# Revit family: RAR3
name_source: partatom
category: Lighting Fixtures
revit_build: Autodesk Revit 2014 (Build: 20130308_1515(x64)
units: mm (PartAtom-declared; Revit-internal decimal feet)

## types (1)
- RAR3
    Apparent Load = 40 VA
    Assembly Code = D5020200
    Center Width = 3 "
    Certifications = UL,CSA,Wet Listed, Damp Listed, ANSI 3G Vibration Rated
    Color Filter = 16777215
    Color Temperature = 0 K
    Depth = 18.44 "
    Description = With a new spin on a classic rectilinear form, Ratio brings the traditional shoebox aesthetic into the next generation of LED lighting. Ratio features a dense optical array which provides reduced pixilation and increased visual comfort without compromising performance. Designed for sustained, long-term performance with advanced thermal management, an elegantly simple heat sink, and industry leading surge protection.
    Dimming Lamp Color Temperature Shift = <None>
    Emit Shape Visible in Rendering = No
    Emit from Rectangle Length = 15 "
    Emit from Rectangle Width = 15 "
    Features = • Low profile LED area/site luminaire with a variety of IES distributions for
lighting applications such as retail, commercial and campus parking lots
• Featuring Micro Strike Optics which maximizes target zone illumination with
minimal losses at the house-side, reducing light trespass issues
• Visual comfort standard
• Area and flood optics available for maximum versatility
• Control options including photo control, occupancy sensing, NX Distributed
Intelligence™ and 7-Pin with networked controls
• Best in class surge protection
    Finish = Powder Coat-Hubbell-Black
    Fixture Height = 7.5 "
    Lamp = default
    Lens = Glass-Hubbell-Temper Molded
    Manufacturer = Hubbell Lighting
    Model = RAR3
    Number of Poles = 1
    Offset From Pole = 6.12 "
    Photometric Notes = More IES files download on Photometric Web Link
    Photometric Web File = RAR3-720L-375-4K7-3-BC.ies
    Photometric Web Link = https://www.hubbell.com
    Pole = Yes
    Pole Width = 4 "
    Power Factor = 1
    Product Documentation Link = https://hubbellcdn.com
    Product Page URL = https://www.hubbell.com
    Series = Ratio
    Tilt Angle = 90.00°
    Type Comments = Lighting Fixture
    URL = https://www.hubbell.com
    Voltage = 0 V
    Wattage Comments = 40
    Width = 14 "

## geometry (parser evidence)
native form markers: Blend x2, Sweep x5
no freeform markers — native parametric forms only
